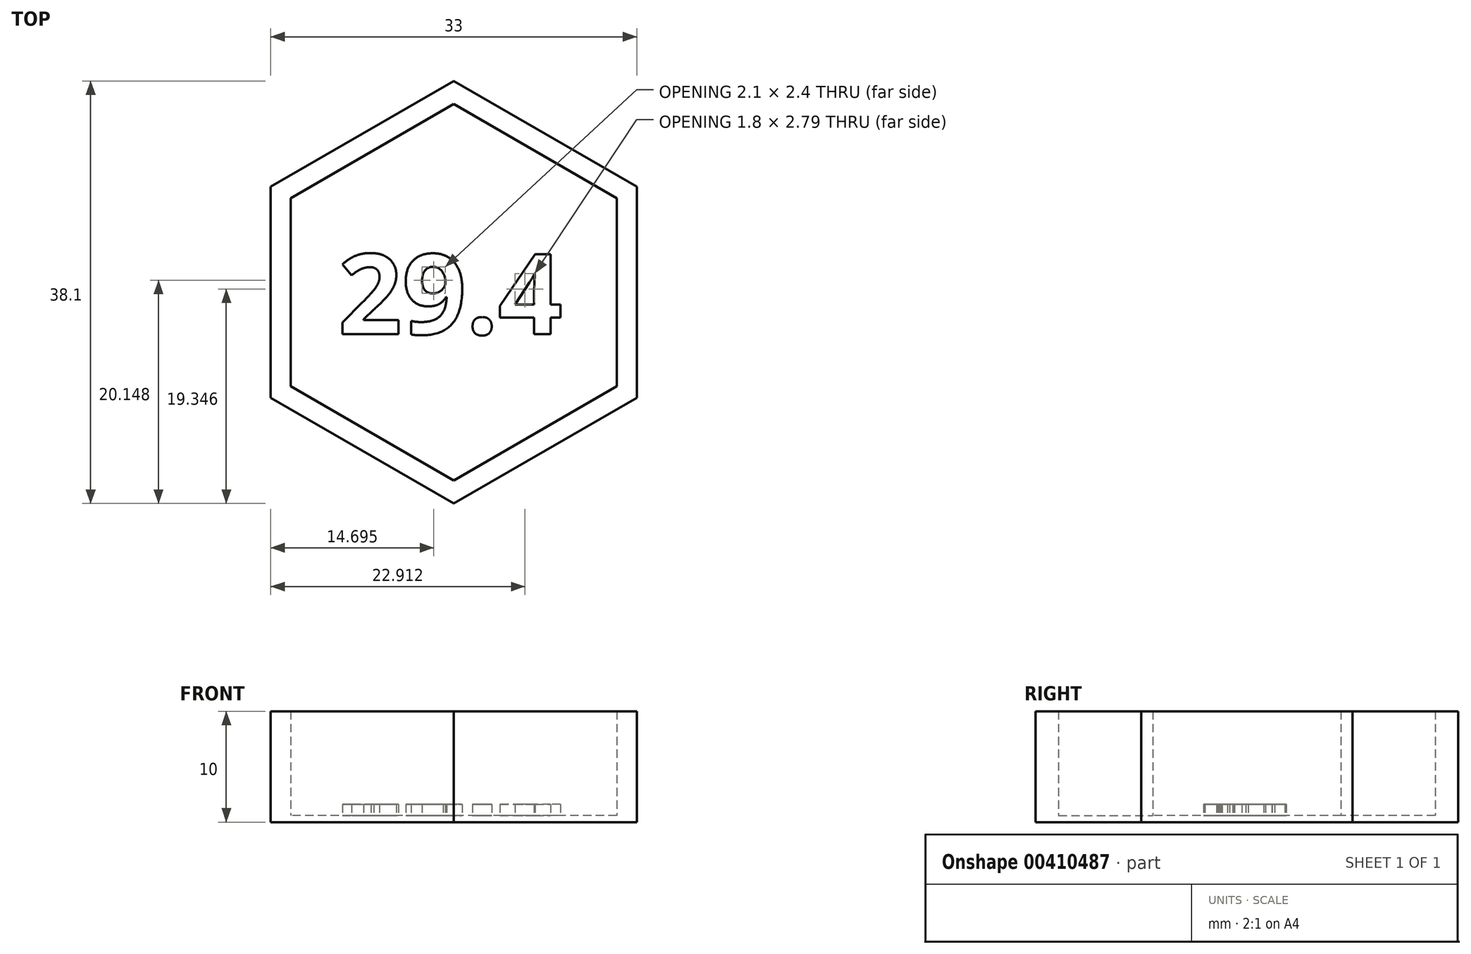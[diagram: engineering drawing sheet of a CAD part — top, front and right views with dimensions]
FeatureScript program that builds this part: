
annotation { "Feature Type Name" : "Feature", "Feature Type Description" : "" }
export const myFeature = defineFeature(function(context is Context, id is Id, definition is map)
    precondition{}
    {
        {
            var Q0;
            Q0=qCreatedBy(makeId("Top.planeOp"),FACE);
            cPlane(context, id + "F0", {"entities" : qUnion([Q0]), "cplaneType" : CPlaneType.OFFSET, "offset" : 0.6 * mm, "oppositeDirection" : true, "width" : 150 * mm, "height" : 150 * mm});
        }
        {
            var Q0;
            Q0=qCreatedBy(id+"F0.planeOp",FACE);
            var sketch = newSketch(context, id + "F1", { "sketchPlane" : qUnion([Q0])});
            skCircle(sketch, "E0.cCircle", {"center": v(0, 0) * mm, "radius": 19.05 * mm, "construction": true});
            skLineSegment(sketch, "E0.0", {"start": v(16.5, -9.53) * mm, "end": v(0, -19.05) * mm});
            skLineSegment(sketch, "E0.1", {"start": v(0, -19.05) * mm, "end": v(-16.5, -9.53) * mm});
            skLineSegment(sketch, "E0.2", {"start": v(-16.5, -9.53) * mm, "end": v(-16.5, 9.53) * mm});
            skLineSegment(sketch, "E0.3", {"start": v(-16.5, 9.53) * mm, "end": v(0, 19.05) * mm});
            skLineSegment(sketch, "E0.4", {"start": v(0, 19.05) * mm, "end": v(16.5, 9.53) * mm});
            skLineSegment(sketch, "E0.5", {"start": v(16.5, 9.53) * mm, "end": v(16.5, -9.53) * mm});
            skSolve(sketch);
        }
        {
            var Q0;
            Q0=makeQuery(id+"F1.imprint","IMPRINT",FACE,{"disambiguationData":[TD([[makeQuery(id+"F1.imprint","IMPRINT",EDGE,{"derivedFrom":sQuery(id+"F1.wireOp",EDGE,"E0.0")}),-1.0]])]});
            extrude(context, id + "F2", {"entities" : qUnion([Q0]), "depth" : 10 * mm});
        }
        {
            var Q0;
            Q0=qCreatedBy(makeId("Top.planeOp"),FACE);
            var sketch = newSketch(context, id + "F3", { "sketchPlane" : qUnion([Q0])});
            skCircle(sketch, "E1.cCircle", {"center": v(0, 0) * mm, "radius": 16.97 * mm, "construction": true});
            skLineSegment(sketch, "E1.0", {"start": v(0, -16.97) * mm, "end": v(-14.7, -8.49) * mm});
            skLineSegment(sketch, "E1.1", {"start": v(-14.7, -8.49) * mm, "end": v(-14.7, 8.49) * mm});
            skLineSegment(sketch, "E1.2", {"start": v(-14.7, 8.49) * mm, "end": v(0, 16.97) * mm});
            skLineSegment(sketch, "E1.3", {"start": v(0, 16.97) * mm, "end": v(14.7, 8.49) * mm});
            skLineSegment(sketch, "E1.4", {"start": v(14.7, 8.49) * mm, "end": v(14.7, -8.49) * mm});
            skLineSegment(sketch, "E1.5", {"start": v(14.7, -8.49) * mm, "end": v(0, -16.97) * mm});
            skSolve(sketch);
        }
        {
            var Q0;
            Q0=makeQuery(id+"F3.imprint","IMPRINT",FACE,{"disambiguationData":[TD([[makeQuery(id+"F3.imprint","IMPRINT",EDGE,{"derivedFrom":sQuery(id+"F3.wireOp",EDGE,"E1.0")}),-1.0]])]});
            extrude(context, id + "F4", {"entities" : qUnion([Q0]), "operationType" : NewBodyOperationType.REMOVE, "depth" : 25 * mm});
        }
        {
            var Q0;
            Q0=qCreatedBy(makeId("Top.planeOp"),FACE);
            var sketch = newSketch(context, id + "F5", { "sketchPlane" : qUnion([Q0])});
            skText(sketch, "E2", { "text": "29.4\n", "fontName": "OpenSans-Bold.ttf"});
            const initialGuessF5  = {"E2": [-0.01043, -0.00378, 1, 0, 0.00728]};
            skSetInitialGuess(sketch, initialGuessF5);
            skSolve(sketch);
        }
        {
            var Q0;
            Q0=qSketchRegion(id+"F5",true);
            extrude(context, id + "F6", {"entities" : qUnion([Q0]), "depth" : 1 * mm});
        }
    });
